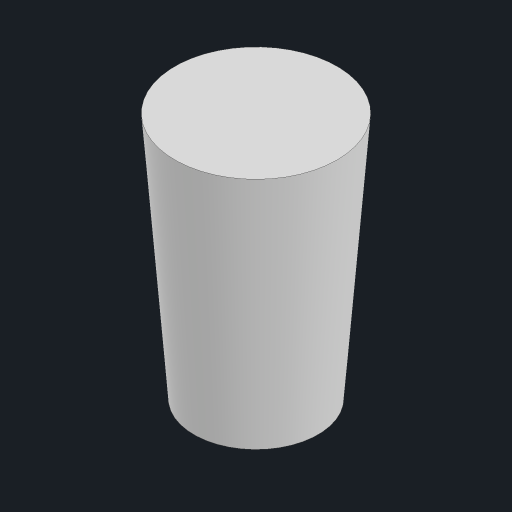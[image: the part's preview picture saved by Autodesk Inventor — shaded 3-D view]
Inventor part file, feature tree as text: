
AUTODESK INVENTOR PART (.ipt)
format: ipt  version: 2023.1 (Build 271208000, 208)  size: 102,912 bytes
history: native  units: mm
features: sketch x2, plane x2, loft x1
ambient origin geometry x8: Origin, YZ Plane, XZ Plane, XY Plane, X Axis, Y Axis, Z Axis, Center Point
bodies: Body1 (feature_tree)
feature tree (5):
  sketch  "Sketch1"  dims[d0=17.0mm d4=25.94mm]
  plane  "Work Plane1"
  plane  "Work Plane2"
  loft  "Loft1"
  sketch  "Sketch4"  dims[d5=13.0mm d6=0.0mm d7=90.0deg d8=0.0mm d9=90.0deg]
